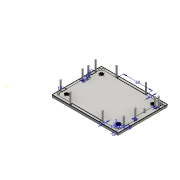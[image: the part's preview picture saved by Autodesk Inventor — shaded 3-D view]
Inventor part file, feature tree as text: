
AUTODESK INVENTOR PART (.ipt)
format: ipt  version: 2016 (Build 200138000, 138)  size: 356,864 bytes
history: native  units: mm
features: extrude x6, sketch x2, hole x2, other x2, fillet x2, pattern_linear x1
ambient origin geometry x8: Origin, YZ Plane, XZ Plane, XY Plane, X Axis, Y Axis, Z Axis, Center Point
bodies: Solid1 (feature_tree)
feature tree (15):
  sketch  "Sketch1"  dims[d9=60.0mm d10=5.0mm]
  hole  "HOLES1"  [1 undecoded]
  other  "OUTLINE1"
  other  "OUTLINE2"
  extrude  "Extrusion2"  Depth=5.0mm TaperAngle=0.0deg
  fillet  "Fillet1"  Radius=0.5mm
  extrude  "Extrusion7"  Depth=6.0mm
  fillet  "Fillet3"  Radius=3.0mm
  extrude  "Extrusion8"  Depth=6.0mm
  extrude  "Extrusion9"  Depth=6.0mm
  pattern_linear  "Rectangular Pattern2"  Spacing1=3.0mm  [1 undecoded]
  sketch  "Sketch8"  dims[d11=5.0mm d14=5.0mm d15=0.0mm d36=0.5mm d44=3.0mm d45=3.0mm d46=3.0mm d47=3.0mm d48=3.0mm d49=3.0mm d50=3.0mm d51=3.0mm d52=10.0mm d53=10.0mm d56=10.0mm d57=10.0mm d58=0.0mm d59=0.5mm d62=5.0mm d63=2.85mm d64=1.0mm d65=60.0mm d67=360.0deg d69=2.3mm d70=0.0mm d71=5.0mm d72=10.0mm d73=0.0mm d74=20.0mm d76=72.0mm d77=20.0mm d79=107.0mm d80=3.0mm d81=30.0mm d82=1.8mm d83=3.0mm d84=30.0mm d85=1.8mm d86=3.0mm d87=3.0mm d88=3.0mm d90=3.0mm d91=3.0mm d92=3.0mm d93=3.0mm d94=3.0mm d95=3.0mm d96=3.0mm d97=1.8mm d98=10.0mm d99=1.8mm d100=10.0mm d101=1.8mm d102=5.0mm d103=1.8mm d104=5.0mm d105=3.0mm d106=1.8mm d107=33.0mm d108=1.8mm d109=5.0mm d110=1.8mm d111=5.0mm d112=1.8mm d113=10.0mm d114=1.8mm d115=30.0mm d116=1.8mm d117=30.0mm d118=1.8mm d119=10.0mm d120=3.0mm d121=1.8mm d122=33.0mm d123=3.0mm d124=6.0mm d125=4.0mm d126=2.0mm d127=90.0deg d128=8.0mm d129=20.594885mm d130=20.0mm d131=0.0mm d132=6.0mm d133=0.0mm]
  hole  "Hole1"  [1 undecoded]
  extrude  "Extrusion10"  Depth=6.0mm
  extrude  "Extrusion11"  Depth=6.0mm
note: 3 required parameter values undecoded (feature->parameter linkage not recoverable at this tier; creation-order binding heuristic only, values carry confidence <= 0.55)
